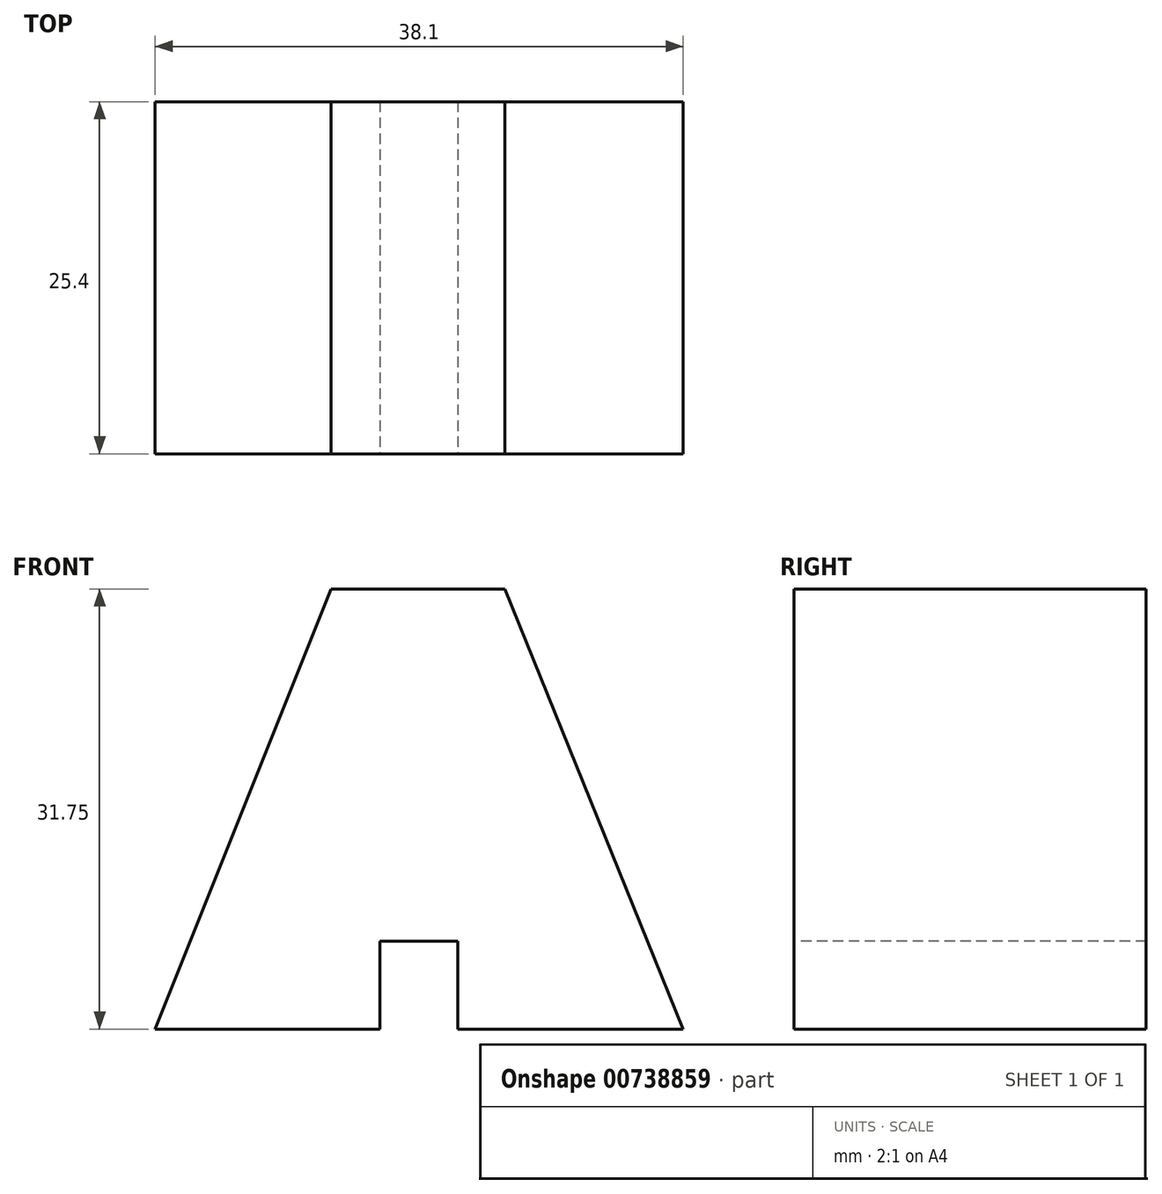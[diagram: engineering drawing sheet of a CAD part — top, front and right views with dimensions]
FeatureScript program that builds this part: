
annotation { "Feature Type Name" : "Feature", "Feature Type Description" : "" }
export const myFeature = defineFeature(function(context is Context, id is Id, definition is map)
    precondition{}
    {
        {
            var Q0;
            Q0=qCreatedBy(makeId("Front.planeOp"),FACE);
            var sketch = newSketch(context, id + "F0", { "sketchPlane" : qUnion([Q0])});
            skLineSegment(sketch, "E0", {"start": v(0, 31.75) * mm, "end": v(0, 0) * mm});
            skLineSegment(sketch, "E1", {"start": v(0, 0) * mm, "end": v(38.1, 0) * mm});
            skLineSegment(sketch, "E2", {"start": v(38.1, 0) * mm, "end": v(38.1, 31.75) * mm});
            skLineSegment(sketch, "E3", {"start": v(38.1, 31.75) * mm, "end": v(0, 31.75) * mm});
            skSolve(sketch);
        }
        {
            var Q0;
            Q0 = qSketchRegion(id + "F0", true);
            extrude(context, id + "F1", {"entities" : qUnion([Q0]), "depth" : 25.4 * mm, "offsetDistance" : 25.4 * mm});
        }
        {
            var Q0;
            Q0=makeQuery(id+"F1.opExtrude","CAP_FACE",FACE,{"disambiguationData":[OSD([sQuery(id+"F0.wireOp",EDGE,"E0"),sQuery(id+"F0.wireOp",EDGE,"E1"),sQuery(id+"F0.wireOp",EDGE,"E2"),sQuery(id+"F0.wireOp",EDGE,"E3")])],"isStart":false});
            var sketch = newSketch(context, id + "F2", { "sketchPlane" : qUnion([Q0])});
            skLineSegment(sketch, "E4", {"start": v(16.22, 0) * mm, "end": v(16.22, 6.35) * mm});
            skLineSegment(sketch, "E5", {"start": v(16.22, 6.35) * mm, "end": v(21.82, 6.35) * mm});
            skLineSegment(sketch, "E6", {"start": v(21.82, 6.35) * mm, "end": v(21.82, 0) * mm});
            skLineSegment(sketch, "E7", {"start": v(21.82, 0) * mm, "end": v(16.22, 0) * mm});
            skLineSegment(sketch, "E8", {"start": v(12.7, 31.75) * mm, "end": v(0, 0) * mm});
            skLineSegment(sketch, "E9", {"start": v(25.23, 31.75) * mm, "end": v(38.1, 0) * mm});
            skLineSegment(sketch, "E10", {"start": v(12.7, 31.75) * mm, "end": v(0, 31.75) * mm});
            skLineSegment(sketch, "E11", {"start": v(25.23, 31.75) * mm, "end": v(38.1, 31.75) * mm});
            skSolve(sketch);
        }
        {
            var Q0;
            Q0 = qSketchRegion(id + "F2", true);
            var Q1;
            Q1=makeQuery(id+"F2.imprint","IMPRINT",FACE,{"disambiguationData":[TD([[makeQuery(id+"F2.imprint","IMPRINT",EDGE,{"derivedFrom":sQuery(id+"F2.wireOp",EDGE,"E8")}),-1.0]])]});
            var Q2;
            Q2=makeQuery(id+"F2.imprint","IMPRINT",FACE,{"disambiguationData":[TD([[makeQuery(id+"F2.imprint","IMPRINT",EDGE,{"derivedFrom":sQuery(id+"F2.wireOp",EDGE,"E9")}),1.0]])]});
            extrude(context, id + "F3", {"entities" : qUnion([Q0, Q1, Q2]), "operationType" : NewBodyOperationType.REMOVE, "oppositeDirection" : true, "depth" : 25.4 * mm, "offsetDistance" : 25.4 * mm});
        }
    });
